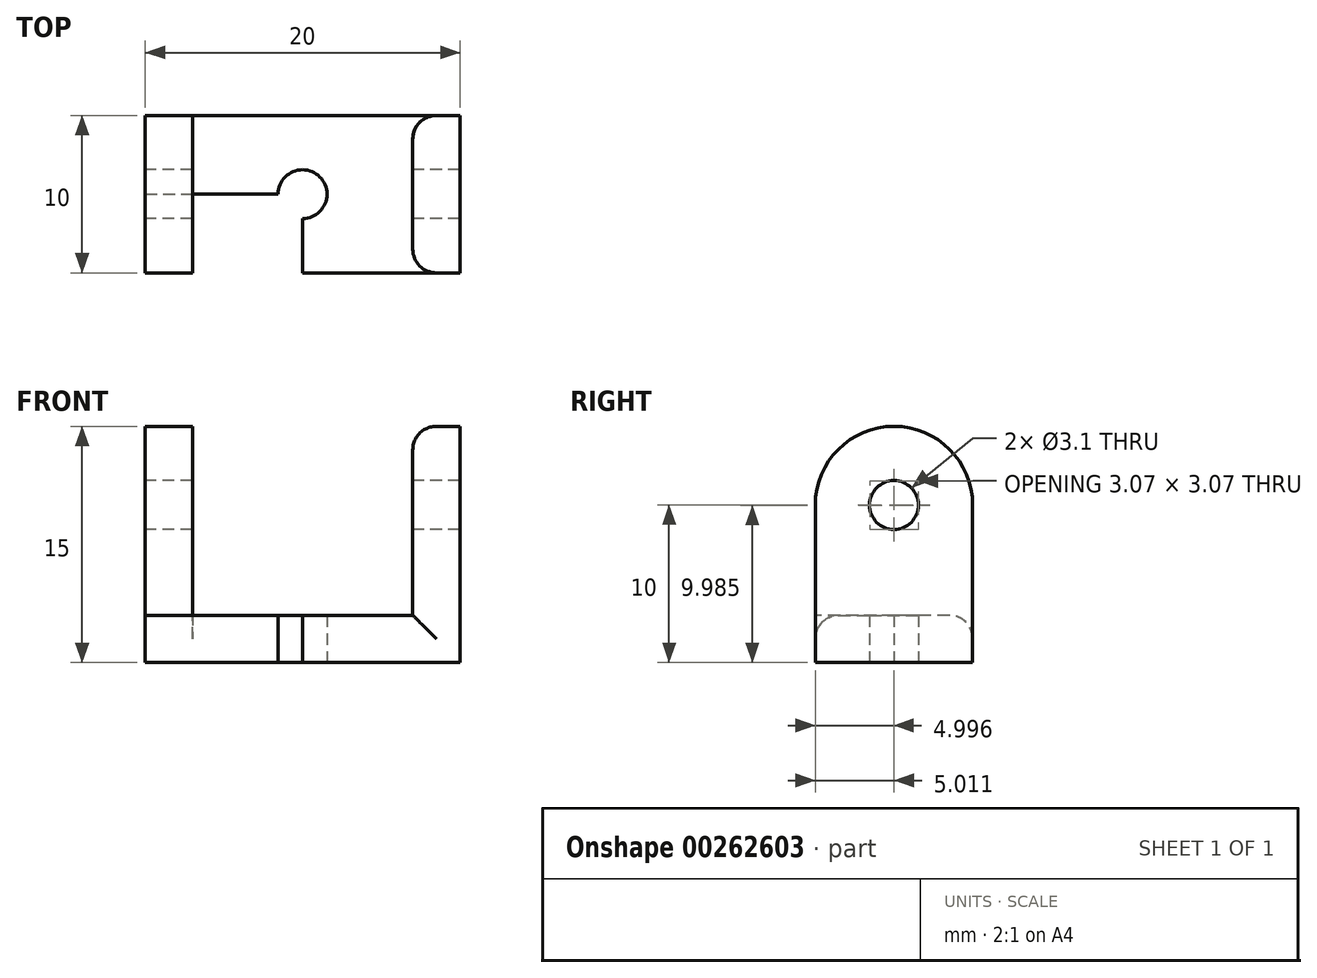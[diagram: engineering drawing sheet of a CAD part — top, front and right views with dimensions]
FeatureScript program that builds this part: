
annotation { "Feature Type Name" : "Feature", "Feature Type Description" : "" }
export const myFeature = defineFeature(function(context is Context, id is Id, definition is map)
    precondition{}
    {
        {
            var Q0;
            Q0=qCreatedBy(makeId("Top.planeOp"),FACE);
            var sketch = newSketch(context, id + "F0", { "sketchPlane" : qUnion([Q0])});
            skLineSegment(sketch, "E0.bottom", {"start": v(-2.74, -2.4) * mm, "end": v(17.26, -2.4) * mm});
            skLineSegment(sketch, "E0.top", {"start": v(-2.74, -12.4) * mm, "end": v(17.26, -12.4) * mm});
            skLineSegment(sketch, "E0.left", {"start": v(-2.74, -2.4) * mm, "end": v(-2.74, -12.4) * mm});
            skLineSegment(sketch, "E0.right", {"start": v(17.26, -2.4) * mm, "end": v(17.26, -12.4) * mm});
            skLineSegment(sketch, "E1.bottom", {"start": v(-2.74, -12.4) * mm, "end": v(7.26, -12.4) * mm});
            skLineSegment(sketch, "E1.top", {"start": v(-2.74, -7.4) * mm, "end": v(7.26, -7.4) * mm});
            skLineSegment(sketch, "E1.left", {"start": v(-2.74, -12.4) * mm, "end": v(-2.74, -7.4) * mm});
            skLineSegment(sketch, "E1.right", {"start": v(7.26, -12.4) * mm, "end": v(7.26, -7.4) * mm});
            skCircle(sketch, "E2", {"center": v(7.26, -7.4) * mm, "radius": 1.55 * mm});
            skSolve(sketch);
        }
        {
            var Q0;
            {var subQ1=sQuery(id+"F0.wireOp",EDGE,"E1.bottom");Q0=makeQuery(id+"F0.imprint","IMPRINT",FACE,{"disambiguationData":[TD([[makeQuery(id+"F0.imprint","IMPRINT",EDGE,{"derivedFrom":subQ1}),1.0]])]});}
            var Q1;
            Q1=makeQuery(id+"F0.imprint","IMPRINT",FACE,{"disambiguationData":[TD([[makeQuery(id+"F0.imprint","IMPRINT",EDGE,{"derivedFrom":sQuery(id+"F0.wireOp",EDGE,"E0.bottom")}),-1.0]])]});
            extrude(context, id + "F1", {"entities" : qUnion([Q0, Q1]), "depth" : 3 * mm});
        }
        {
            var Q0;
            Q0=makeQuery(id+"F1.opExtrude","CAP_FACE",FACE,{"disambiguationData":[OSD([sQuery(id+"F0.wireOp",EDGE,"E0.bottom"),sQuery(id+"F0.wireOp",EDGE,"E0.top"),sQuery(id+"F0.wireOp",EDGE,"E0.left"),sQuery(id+"F0.wireOp",EDGE,"E0.right"),sQuery(id+"F0.wireOp",EDGE,"E1.bottom"),sQuery(id+"F0.wireOp",EDGE,"E1.left"),sQuery(id+"F0.wireOp",EDGE,"E2")])],"isStart":false});
            var sketch = newSketch(context, id + "F2", { "sketchPlane" : qUnion([Q0])});
            skLineSegment(sketch, "E3.bottom", {"start": v(-2.74, -2.4) * mm, "end": v(0.26, -2.4) * mm});
            skLineSegment(sketch, "E3.top", {"start": v(-2.74, -12.4) * mm, "end": v(0.26, -12.4) * mm});
            skLineSegment(sketch, "E3.left", {"start": v(-2.74, -2.4) * mm, "end": v(-2.74, -12.4) * mm});
            skLineSegment(sketch, "E3.right", {"start": v(0.26, -2.4) * mm, "end": v(0.26, -12.4) * mm});
            skLineSegment(sketch, "E4.bottom", {"start": v(17.26, -2.4) * mm, "end": v(14.26, -2.4) * mm});
            skLineSegment(sketch, "E4.top", {"start": v(17.26, -12.4) * mm, "end": v(14.26, -12.4) * mm});
            skLineSegment(sketch, "E4.left", {"start": v(17.26, -2.4) * mm, "end": v(17.26, -12.4) * mm});
            skLineSegment(sketch, "E4.right", {"start": v(14.26, -2.4) * mm, "end": v(14.26, -12.4) * mm});
            skSolve(sketch);
        }
        {
            var Q0;
            Q0 = qSketchRegion(id + "F2", true);
            extrude(context, id + "F3", {"entities" : qUnion([Q0]), "operationType" : NewBodyOperationType.ADD, "depth" : 12 * mm});
        }
        {
            var Q0;
            Q0=makeQuery(id+"F3.boolean.opBoolean","MERGE",FACE,{"derivedFrom":[makeQuery(id+"F1.opExtrude","SWEPT_FACE",FACE,{"disambiguationData":[OSD([sQuery(id+"F0.wireOp",EDGE,"E0.left"),sQuery(id+"F0.wireOp",EDGE,"E1.left")])]}),makeQuery(id+"F3.opExtrude","SWEPT_FACE",FACE,{"disambiguationData":[OSD([sQuery(id+"F2.wireOp",EDGE,"E3.left")])]})]});
            var sketch = newSketch(context, id + "F4", { "sketchPlane" : qUnion([Q0])});
            skLineSegment(sketch, "E5.bottom", {"start": v(2.4, 0) * mm, "end": v(7.4, 0) * mm});
            skLineSegment(sketch, "E5.top", {"start": v(2.4, 10) * mm, "end": v(7.4, 10) * mm});
            skLineSegment(sketch, "E5.left", {"start": v(2.4, 0) * mm, "end": v(2.4, 10) * mm});
            skLineSegment(sketch, "E5.right", {"start": v(7.4, 0) * mm, "end": v(7.4, 10) * mm});
            skCircle(sketch, "E6", {"center": v(7.4, 10) * mm, "radius": 1.55 * mm});
            skSolve(sketch);
        }
        {
            var Q0;
            {var subQ0=sQuery(id+"F4.wireOp",EDGE,"E5.right");var subQ1=sQuery(id+"F4.wireOp",EDGE,"E5.top");var subQ2=makeQuery(id+"F4.imprint","INTERSECT",VERTEX,{"derivedFrom":[subQ1,subQ0]});Q0=makeQuery(id+"F4.imprint","IMPRINT",FACE,{"disambiguationData":[TD([[makeQuery(id+"F4.imprint","IMPRINT",EDGE,{"disambiguationData":[TD([[subQ2,1.0]])],"derivedFrom":subQ1}),-1.0]])]});}
            var Q1;
            {var subQ0=sQuery(id+"F4.wireOp",EDGE,"E5.right");var subQ1=sQuery(id+"F4.wireOp",EDGE,"E5.top");var subQ2=makeQuery(id+"F4.imprint","INTERSECT",VERTEX,{"derivedFrom":[subQ1,subQ0]});Q1=makeQuery(id+"F4.imprint","IMPRINT",FACE,{"disambiguationData":[TD([[makeQuery(id+"F4.imprint","IMPRINT",EDGE,{"disambiguationData":[TD([[subQ2,1.0]])],"derivedFrom":subQ1}),1.0]])]});}
            extrude(context, id + "F5", {"entities" : qUnion([Q0, Q1]), "operationType" : NewBodyOperationType.REMOVE, "oppositeDirection" : true, "depth" : 25 * mm});
        }
        {
            var Q0;
            Q0=makeQuery(id+"F3.opExtrude","CAP_EDGE",EDGE,{"disambiguationData":[OSD([sQuery(id+"F2.wireOp",EDGE,"E3.bottom")])],"isStart":false});
            var Q1;
            Q1=makeQuery(id+"F3.opExtrude","CAP_EDGE",EDGE,{"disambiguationData":[OSD([sQuery(id+"F2.wireOp",EDGE,"E4.bottom")])],"isStart":false});
            var Q2;
            Q2=makeQuery(id+"F3.opExtrude","CAP_EDGE",EDGE,{"disambiguationData":[OSD([sQuery(id+"F2.wireOp",EDGE,"E4.top")])],"isStart":false});
            var Q3;
            Q3=makeQuery(id+"F3.opExtrude","CAP_EDGE",EDGE,{"disambiguationData":[OSD([sQuery(id+"F2.wireOp",EDGE,"E3.top")])],"isStart":false});
            fillet(context, id + "F6", {"entities" : qUnion([Q0, Q1, Q2, Q3]), "radius" : 5 * mm, "tangentPropagation" : true, "allowEdgeOverflow" : false});
        }
        {
            var Q0;
            Q0=makeQuery(id+"F1.opExtrude","CAP_EDGE",EDGE,{"disambiguationData":[OSD([sQuery(id+"F0.wireOp",EDGE,"E0.bottom")])],"isStart":false});
            var Q1;
            Q1=makeQuery(id+"F1.opExtrude","CAP_EDGE",EDGE,{"disambiguationData":[OSD([sQuery(id+"F0.wireOp",EDGE,"E0.top"),sQuery(id+"F0.wireOp",EDGE,"E1.bottom")])],"isStart":false});
            var Q2;
            Q2=makeQuery(id+"F6.opFillet","BLEND_EDGE",EDGE,{"blendedFrom":[makeQuery(id+"F3.opExtrude","CAP_EDGE",EDGE,{"disambiguationData":[OSD([sQuery(id+"F2.wireOp",EDGE,"E3.top")])],"isStart":false}),makeQuery(id+"F3.opExtrude","SWEPT_FACE",FACE,{"disambiguationData":[OSD([sQuery(id+"F2.wireOp",EDGE,"E3.right")])]})],"blendedInto":[makeQuery(id+"F3.opExtrude","SWEPT_FACE",FACE,{"disambiguationData":[OSD([sQuery(id+"F2.wireOp",EDGE,"E3.right")])]})]});
            var Q3;
            Q3=makeQuery(id+"F6.opFillet","BLEND_EDGE",EDGE,{"blendedFrom":[makeQuery(id+"F3.opExtrude","CAP_EDGE",EDGE,{"disambiguationData":[OSD([sQuery(id+"F2.wireOp",EDGE,"E4.bottom")])],"isStart":false}),makeQuery(id+"F3.opExtrude","SWEPT_FACE",FACE,{"disambiguationData":[OSD([sQuery(id+"F2.wireOp",EDGE,"E4.right")])]})],"blendedInto":[makeQuery(id+"F3.opExtrude","SWEPT_FACE",FACE,{"disambiguationData":[OSD([sQuery(id+"F2.wireOp",EDGE,"E4.right")])]})]});
            fillet(context, id + "F7", {"entities" : qUnion([Q0, Q1, Q2, Q3]), "radius" : 1.5 * mm, "tangentPropagation" : true, "allowEdgeOverflow" : false});
        }
    });
